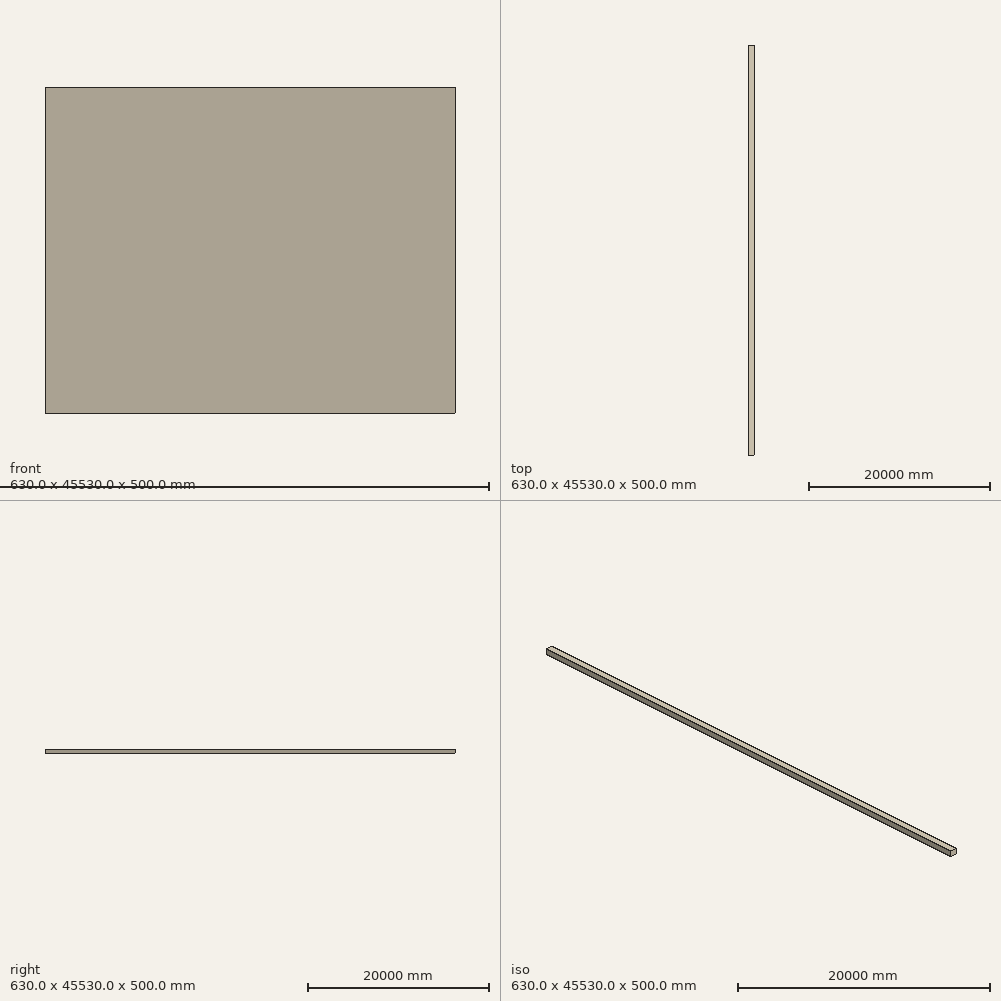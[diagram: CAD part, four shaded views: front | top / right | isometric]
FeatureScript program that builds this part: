
annotation { "Feature Type Name" : "Feature", "Feature Type Description" : "" }
export const myFeature = defineFeature(function(context is Context, id is Id, definition is map)
    precondition{}
    {
        {
            var Q0;
            Q0=qCreatedBy(makeId("Top.planeOp"),FACE);
            var sketch = newSketch(context, id + "F0", { "sketchPlane" : qUnion([Q0])});
            skLineSegment(sketch, "E0.bottom", {"start": v(-315, 0) * mm, "end": v(315, 0) * mm});
            skLineSegment(sketch, "E0.top", {"start": v(-315, 45530) * mm, "end": v(315, 45530) * mm});
            skLineSegment(sketch, "E0.left", {"start": v(-315, 0) * mm, "end": v(-315, 45530) * mm});
            skLineSegment(sketch, "E0.right", {"start": v(315, 0) * mm, "end": v(315, 45530) * mm});
            skSolve(sketch);
        }
        {
            var Q0;
            Q0=makeQuery(id+"F0.imprint","IMPRINT",FACE,{"disambiguationData":[TD([[makeQuery(id+"F0.imprint","IMPRINT",EDGE,{"derivedFrom":sQuery(id+"F0.wireOp",EDGE,"E0.bottom")}),1.0]])]});
            extrude(context, id + "F1", {"entities" : qUnion([Q0]), "oppositeDirection" : true, "depth" : 500 * mm, "offsetDistance" : 25.4 * mm});
        }
    });
